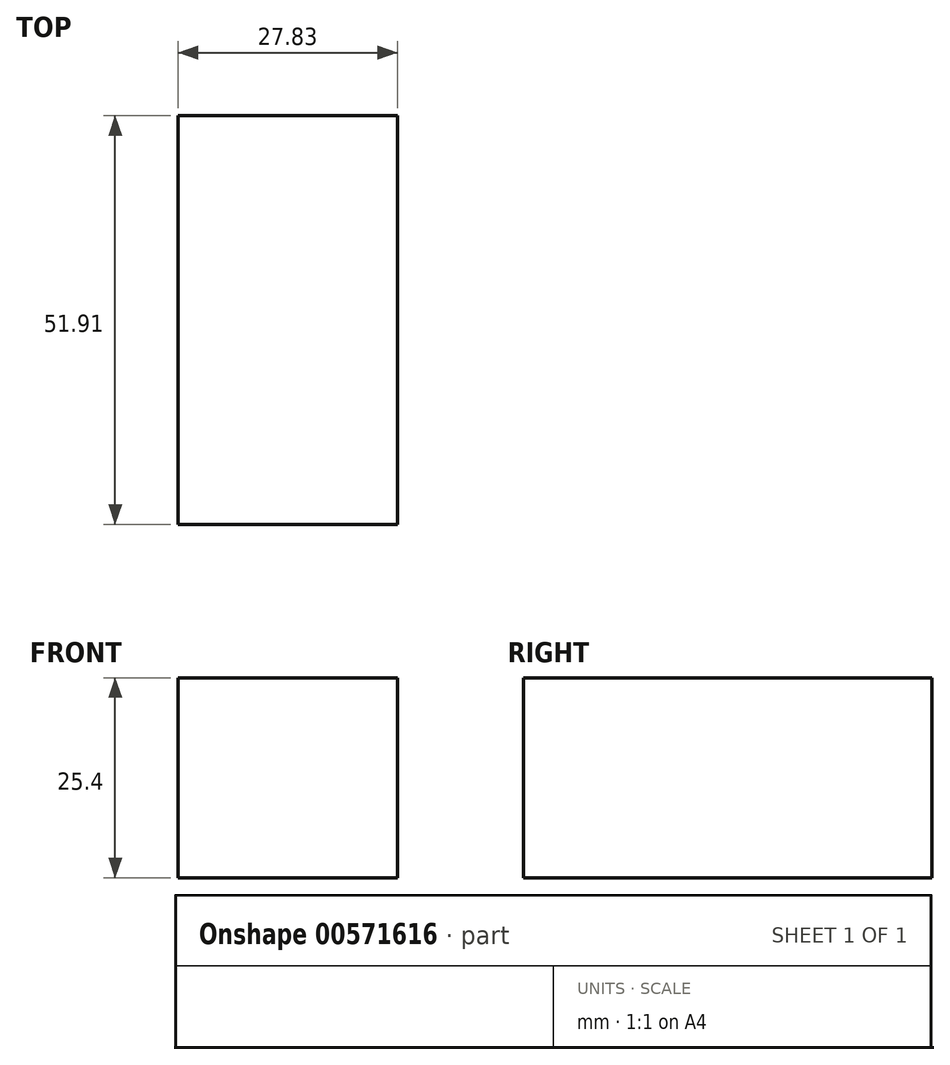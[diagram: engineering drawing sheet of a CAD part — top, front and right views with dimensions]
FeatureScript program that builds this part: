
annotation { "Feature Type Name" : "Feature", "Feature Type Description" : "" }
export const myFeature = defineFeature(function(context is Context, id is Id, definition is map)
    precondition{}
    {
        {
            var Q0;
            Q0=qCreatedBy(makeId("Top.planeOp"),FACE);
            var sketch = newSketch(context, id + "F0", { "sketchPlane" : qUnion([Q0])});
            skLineSegment(sketch, "E0", {"start": v(-49.37, 56.46) * mm, "end": v(32.91, 56.46) * mm});
            skLineSegment(sketch, "E1", {"start": v(-49.37, 56.46) * mm, "end": v(-49.37, 26.39) * mm});
            skLineSegment(sketch, "E2", {"start": v(32.91, 56.46) * mm, "end": v(32.91, 27.52) * mm});
            skLineSegment(sketch, "E3", {"start": v(-49.37, 26.39) * mm, "end": v(26.14, 26.39) * mm});
            skLineSegment(sketch, "E4.bottom", {"start": v(10.41, 26.39) * mm, "end": v(15.55, 26.39) * mm});
            skLineSegment(sketch, "E4.top", {"start": v(10.41, -25.52) * mm, "end": v(15.55, -25.52) * mm});
            skLineSegment(sketch, "E4.left", {"start": v(10.41, 26.39) * mm, "end": v(10.41, -25.52) * mm});
            skLineSegment(sketch, "E4.right", {"start": v(15.55, 26.39) * mm, "end": v(15.55, -25.52) * mm});
            skLineSegment(sketch, "E5.bottom", {"start": v(15.55, -25.52) * mm, "end": v(-17.42, -25.52) * mm});
            skLineSegment(sketch, "E5.top", {"start": v(15.55, 26.39) * mm, "end": v(-17.42, 26.39) * mm});
            skLineSegment(sketch, "E5.left", {"start": v(15.55, -25.52) * mm, "end": v(15.55, 26.39) * mm});
            skLineSegment(sketch, "E5.right", {"start": v(-17.42, -25.52) * mm, "end": v(-17.42, 26.39) * mm});
            skLineSegment(sketch, "E6.bottom", {"start": v(-46.46, 56.46) * mm, "end": v(32.91, 56.46) * mm});
            skLineSegment(sketch, "E6.top", {"start": v(-46.46, 27.52) * mm, "end": v(32.91, 27.52) * mm});
            skLineSegment(sketch, "E6.left", {"start": v(-46.46, 56.46) * mm, "end": v(-46.46, 27.52) * mm});
            skLineSegment(sketch, "E7.bottom", {"start": v(-17.42, -25.52) * mm, "end": v(15.55, -25.52) * mm});
            skLineSegment(sketch, "E7.top", {"start": v(-17.42, -64.24) * mm, "end": v(15.55, -64.24) * mm});
            skLineSegment(sketch, "E7.left", {"start": v(-17.42, -25.52) * mm, "end": v(-17.42, -64.24) * mm});
            skLineSegment(sketch, "E7.right", {"start": v(15.55, -25.52) * mm, "end": v(15.55, -64.24) * mm});
            skSolve(sketch);
        }
        {
            var Q0;
            {var subQ0=sQuery(id+"F0.wireOp",EDGE,"E4.left");Q0=makeQuery(id+"F0.imprint","IMPRINT",FACE,{"disambiguationData":[TD([[makeQuery(id+"F0.imprint","IMPRINT",EDGE,{"derivedFrom":subQ0}),-1.0]])]});}
            extrude(context, id + "F1", {"entities" : qUnion([Q0]), "depth" : 25.4 * mm, "offsetDistance" : 25.4 * mm});
        }
    });
